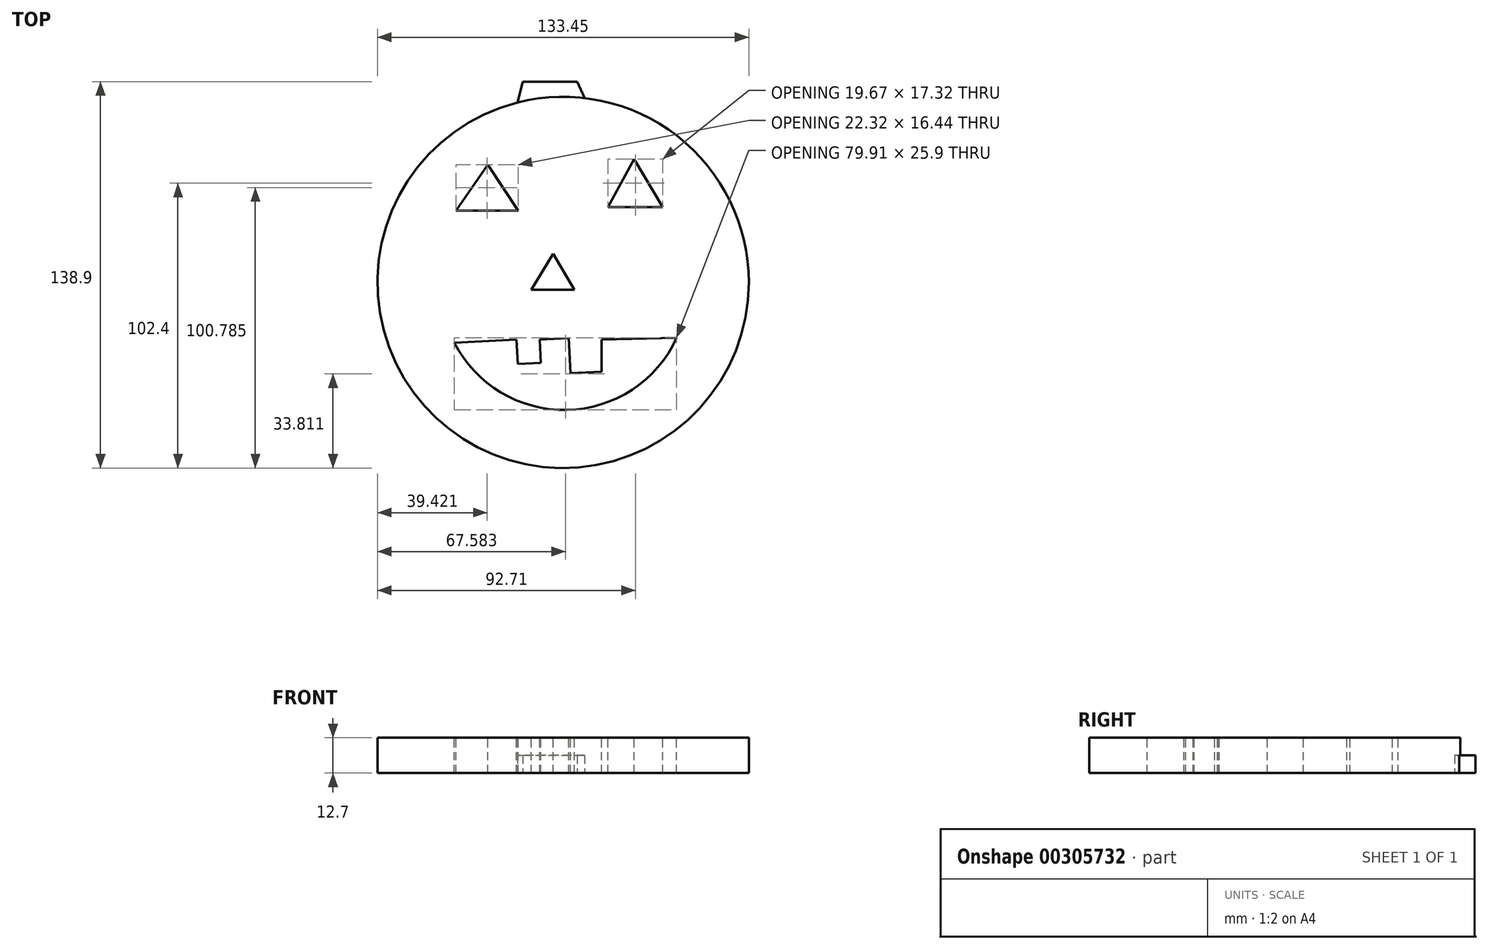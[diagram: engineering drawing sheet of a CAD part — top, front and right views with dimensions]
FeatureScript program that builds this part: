
annotation { "Feature Type Name" : "Feature", "Feature Type Description" : "" }
export const myFeature = defineFeature(function(context is Context, id is Id, definition is map)
    precondition{}
    {
        {
            var Q0;
            Q0=qCreatedBy(makeId("Top.planeOp"),FACE);
            var sketch = newSketch(context, id + "F0", { "sketchPlane" : qUnion([Q0])});
            skCircle(sketch, "E0", {"center": v(-8.51, -3.96) * mm, "radius": 66.73 * mm});
            skSolve(sketch);
        }
        {
            var Q0;
            Q0 = qSketchRegion(id + "F0", true);
            extrude(context, id + "F1", {"entities" : qUnion([Q0]), "depth" : 12.7 * mm});
        }
        {
            var Q0;
            Q0=makeQuery(id+"F1.opExtrude","CAP_FACE",FACE,{"disambiguationData":[OSD([sQuery(id+"F0.wireOp",EDGE,"E0")])],"isStart":false});
            var sketch = newSketch(context, id + "F2", { "sketchPlane" : qUnion([Q0])});
            skLineSegment(sketch, "E1", {"start": v(-35.53, 38.32) * mm, "end": v(-46.98, 21.87) * mm});
            skLineSegment(sketch, "E2", {"start": v(-46.98, 21.87) * mm, "end": v(-24.66, 21.87) * mm});
            skLineSegment(sketch, "E3", {"start": v(-35.53, 38.32) * mm, "end": v(-24.66, 21.87) * mm});
            skSolve(sketch);
        }
        {
            var Q0;
            Q0 = qSketchRegion(id + "F2", true);
            extrude(context, id + "F3", {"entities" : qUnion([Q0]), "operationType" : NewBodyOperationType.REMOVE, "oppositeDirection" : true, "depth" : 25.4 * mm});
        }
        {
            var Q0;
            Q0=makeQuery(id+"F1.opExtrude","CAP_FACE",FACE,{"disambiguationData":[OSD([sQuery(id+"F0.wireOp",EDGE,"E0")])],"isStart":false});
            var sketch = newSketch(context, id + "F4", { "sketchPlane" : qUnion([Q0])});
            skLineSegment(sketch, "E4", {"start": v(17.03, 40.37) * mm, "end": v(7.63, 23.05) * mm});
            skLineSegment(sketch, "E5", {"start": v(7.63, 23.05) * mm, "end": v(27.3, 23.05) * mm});
            skLineSegment(sketch, "E6", {"start": v(27.3, 23.05) * mm, "end": v(17.03, 40.37) * mm});
            skSolve(sketch);
        }
        {
            var Q0;
            Q0=makeQuery(id+"F4.imprint","IMPRINT",FACE,{"disambiguationData":[TD([[makeQuery(id+"F4.imprint","IMPRINT",EDGE,{"derivedFrom":sQuery(id+"F4.wireOp",EDGE,"E4")}),1.0]])]});
            extrude(context, id + "F5", {"entities" : qUnion([Q0]), "operationType" : NewBodyOperationType.REMOVE, "oppositeDirection" : true, "depth" : 25.4 * mm});
        }
        {
            var Q0;
            Q0=makeQuery(id+"F1.opExtrude","CAP_FACE",FACE,{"disambiguationData":[OSD([sQuery(id+"F0.wireOp",EDGE,"E0")])],"isStart":false});
            var sketch = newSketch(context, id + "F6", { "sketchPlane" : qUnion([Q0])});
            skArc(sketch, "E7", {"start": v(-48.15, -24.52) * mm, "mid": v(-7.74, -49.84) * mm, "end": v(32.3, -23.93) * mm});
            skLineSegment(sketch, "E8", {"start": v(-47.61, -25.61) * mm, "end": v(-25.25, -24.52) * mm});
            skLineSegment(sketch, "E9", {"start": v(-25.25, -24.52) * mm, "end": v(-24.82, -33.33) * mm});
            skLineSegment(sketch, "E10", {"start": v(-24.82, -33.33) * mm, "end": v(-16.5, -32.92) * mm});
            skLineSegment(sketch, "E11", {"start": v(-16.5, -32.92) * mm, "end": v(-16.9, -24.52) * mm});
            skLineSegment(sketch, "E12", {"start": v(-16.9, -24.52) * mm, "end": v(-6.47, -24) * mm});
            skLineSegment(sketch, "E13", {"start": v(-6.47, -24) * mm, "end": v(-5.85, -36.57) * mm});
            skLineSegment(sketch, "E14", {"start": v(-5.85, -36.57) * mm, "end": v(5.29, -36.02) * mm});
            skLineSegment(sketch, "E15", {"start": v(5.29, -36.02) * mm, "end": v(5.29, -24.52) * mm});
            skLineSegment(sketch, "E16", {"start": v(5.29, -24.52) * mm, "end": v(32.3, -23.93) * mm});
            skSolve(sketch);
        }
        {
            var Q0;
            {var subQ0=sQuery(id+"F6.wireOp",EDGE,"E8");Q0=makeQuery(id+"F6.imprint","IMPRINT",FACE,{"disambiguationData":[TD([[makeQuery(id+"F6.imprint","IMPRINT",EDGE,{"derivedFrom":subQ0}),-1.0]])]});}
            extrude(context, id + "F7", {"entities" : qUnion([Q0]), "operationType" : NewBodyOperationType.REMOVE, "oppositeDirection" : true, "depth" : 12.7 * mm});
        }
        {
            var Q0;
            Q0=makeQuery(id+"F1.opExtrude","CAP_FACE",FACE,{"disambiguationData":[OSD([sQuery(id+"F0.wireOp",EDGE,"E0")])],"isStart":false});
            var sketch = newSketch(context, id + "F8", { "sketchPlane" : qUnion([Q0])});
            skLineSegment(sketch, "E17", {"start": v(-12.04, 6.31) * mm, "end": v(-19.97, -6.6) * mm});
            skLineSegment(sketch, "E18", {"start": v(-19.97, -6.6) * mm, "end": v(-4.4, -6.6) * mm});
            skLineSegment(sketch, "E19", {"start": v(-4.4, -6.6) * mm, "end": v(-12.04, 6.31) * mm});
            skSolve(sketch);
        }
        {
            var Q0;
            Q0 = qSketchRegion(id + "F8", true);
            extrude(context, id + "F9", {"entities" : qUnion([Q0]), "operationType" : NewBodyOperationType.REMOVE, "oppositeDirection" : true, "depth" : 25.4 * mm});
        }
        {
            var Q0;
            Q0=qCreatedBy(makeId("Top.planeOp"),FACE);
            var sketch = newSketch(context, id + "F10", { "sketchPlane" : qUnion([Q0])});
            skLineSegment(sketch, "E20", {"start": v(-25.04, 60.44) * mm, "end": v(-23.02, 68.2) * mm});
            skLineSegment(sketch, "E21", {"start": v(-23.02, 68.2) * mm, "end": v(-3.45, 68.2) * mm});
            skLineSegment(sketch, "E22", {"start": v(-3.45, 68.2) * mm, "end": v(0, 60.44) * mm});
            skLineSegment(sketch, "E23", {"start": v(0, 60.44) * mm, "end": v(-25.04, 60.44) * mm});
            skSolve(sketch);
        }
        {
            var Q0;
            Q0=makeQuery(id+"F10.imprint","IMPRINT",FACE,{"disambiguationData":[TD([[makeQuery(id+"F10.imprint","IMPRINT",EDGE,{"derivedFrom":sQuery(id+"F10.wireOp",EDGE,"E20")}),-1.0]])]});
            extrude(context, id + "F11", {"entities" : qUnion([Q0]), "operationType" : NewBodyOperationType.ADD, "depth" : 6.35 * mm});
        }
    });
